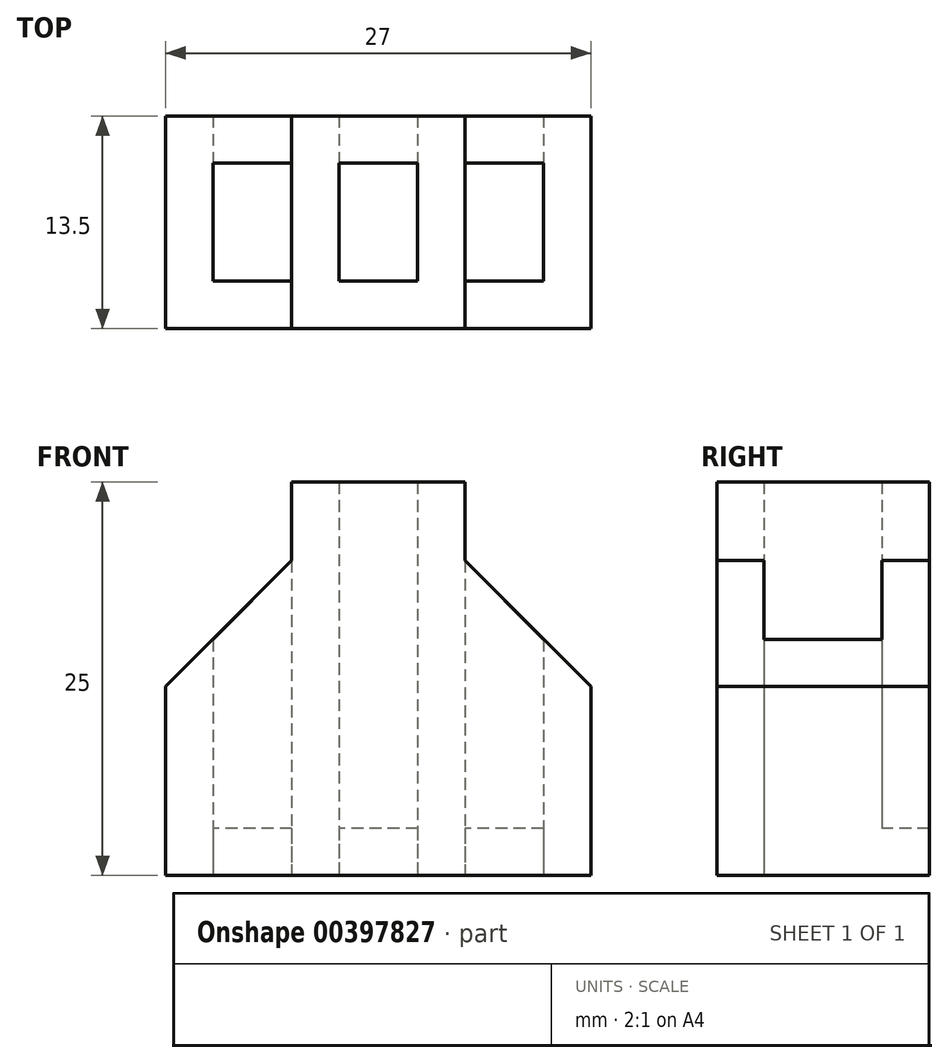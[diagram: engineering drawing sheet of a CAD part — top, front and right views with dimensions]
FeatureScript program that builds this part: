
annotation { "Feature Type Name" : "Feature", "Feature Type Description" : "" }
export const myFeature = defineFeature(function(context is Context, id is Id, definition is map)
    precondition{}
    {
        {
            var Q0;
            Q0=qCreatedBy(makeId("Top.planeOp"),FACE);
            var sketch = newSketch(context, id + "F0", { "sketchPlane" : qUnion([Q0])});
            skLineSegment(sketch, "E0.bottom", {"start": v(-2.5, -3.75) * mm, "end": v(2.5, -3.75) * mm});
            skLineSegment(sketch, "E0.top", {"start": v(-2.5, 3.75) * mm, "end": v(2.5, 3.75) * mm});
            skLineSegment(sketch, "E0.left", {"start": v(-2.5, -3.75) * mm, "end": v(-2.5, 3.75) * mm});
            skLineSegment(sketch, "E0.right", {"start": v(2.5, -3.75) * mm, "end": v(2.5, 3.75) * mm});
            skPoint(sketch, "E0.middle", {"position": v(0, 0) * mm});
            skLineSegment(sketch, "E1.0", {"start": v(-5.5, 6.75) * mm, "end": v(5.5, 6.75) * mm});
            skLineSegment(sketch, "E1.1", {"start": v(-5.5, -3.75) * mm, "end": v(-5.5, 3.75) * mm});
            skLineSegment(sketch, "E1.2", {"start": v(-5.5, -6.75) * mm, "end": v(5.5, -6.75) * mm});
            skLineSegment(sketch, "E1.3", {"start": v(5.5, -3.75) * mm, "end": v(5.5, 3.75) * mm});
            skLineSegment(sketch, "E2", {"start": v(-5.5, 3.75) * mm, "end": v(-10.5, 3.75) * mm});
            skLineSegment(sketch, "E3", {"start": v(-10.5, 3.75) * mm, "end": v(-10.5, -3.75) * mm});
            skLineSegment(sketch, "E4", {"start": v(-10.5, -3.75) * mm, "end": v(-5.5, -3.75) * mm});
            skLineSegment(sketch, "E5.0", {"start": v(-13.5, -6.75) * mm, "end": v(-5.5, -6.75) * mm});
            skLineSegment(sketch, "E5.1", {"start": v(-13.5, 6.75) * mm, "end": v(-13.5, -6.75) * mm});
            skLineSegment(sketch, "E5.2", {"start": v(-5.5, 6.75) * mm, "end": v(-13.5, 6.75) * mm});
            skLineSegment(sketch, "E6.MirrorCS", {"start": v(5.5, 3.75) * mm, "end": v(10.5, 3.75) * mm});
            skLineSegment(sketch, "E7.MirrorCS", {"start": v(10.5, -3.75) * mm, "end": v(5.5, -3.75) * mm});
            skLineSegment(sketch, "E8.MirrorCS", {"start": v(10.5, 3.75) * mm, "end": v(10.5, -3.75) * mm});
            skLineSegment(sketch, "E9.MirrorCS", {"start": v(13.5, -6.75) * mm, "end": v(5.5, -6.75) * mm});
            skLineSegment(sketch, "E10.MirrorCS", {"start": v(13.5, 6.75) * mm, "end": v(13.5, -6.75) * mm});
            skLineSegment(sketch, "E11.MirrorCS", {"start": v(5.5, 6.75) * mm, "end": v(13.5, 6.75) * mm});
            skLineSegment(sketch, "E12", {"start": v(5.5, 3.75) * mm, "end": v(5.5, 6.75) * mm});
            skLineSegment(sketch, "E13", {"start": v(5.5, -3.75) * mm, "end": v(5.5, -6.75) * mm});
            skLineSegment(sketch, "E14", {"start": v(-5.5, -3.75) * mm, "end": v(-5.5, -6.75) * mm});
            skLineSegment(sketch, "E15", {"start": v(-5.5, 3.75) * mm, "end": v(-5.5, 6.75) * mm});
            skSolve(sketch);
        }
        {
            var Q0;
            Q0=makeQuery(id+"F0.imprint","IMPRINT",FACE,{"disambiguationData":[TD([[makeQuery(id+"F0.imprint","IMPRINT",EDGE,{"derivedFrom":sQuery(id+"F0.wireOp",EDGE,"E0.bottom")}),-1.0]])]});
            extrude(context, id + "F1", {"entities" : qUnion([Q0]), "depth" : 25 * mm});
        }
        {
            var Q0;
            Q0=makeQuery(id+"F0.imprint","IMPRINT",FACE,{"disambiguationData":[TD([[makeQuery(id+"F0.imprint","IMPRINT",EDGE,{"derivedFrom":sQuery(id+"F0.wireOp",EDGE,"E2")}),-1.0]])]});
            var Q1;
            Q1=makeQuery(id+"F0.imprint","IMPRINT",FACE,{"disambiguationData":[TD([[makeQuery(id+"F0.imprint","IMPRINT",EDGE,{"derivedFrom":sQuery(id+"F0.wireOp",EDGE,"E6.MirrorCS")}),1.0]])]});
            extrude(context, id + "F2", {"entities" : qUnion([Q0, Q1]), "operationType" : NewBodyOperationType.ADD, "depth" : 20 * mm});
        }
        {
            var Q0;
            Q0=makeQuery(id+"F2.boolean.opBoolean","MERGE",FACE,{"derivedFrom":[makeQuery(id+"F1.opExtrude","SWEPT_FACE",FACE,{"disambiguationData":[OSD([sQuery(id+"F0.wireOp",EDGE,"E1.2")])]}),makeQuery(id+"F2.opExtrude","SWEPT_FACE",FACE,{"disambiguationData":[OSD([sQuery(id+"F0.wireOp",EDGE,"E5.0")])]}),makeQuery(id+"F2.opExtrude","SWEPT_FACE",FACE,{"disambiguationData":[OSD([sQuery(id+"F0.wireOp",EDGE,"E9.MirrorCS")])]})]});
            var sketch = newSketch(context, id + "F3", { "sketchPlane" : qUnion([Q0])});
            skLineSegment(sketch, "E16", {"start": v(-5.5, 20) * mm, "end": v(-13.5, 12) * mm});
            skLineSegment(sketch, "E17.MirrorCS", {"start": v(5.5, 20) * mm, "end": v(13.5, 12) * mm});
            skSolve(sketch);
        }
        {
            var Q0;
            {var subQ0=sQuery(id+"F3.wireOp",EDGE,"E16");Q0=makeQuery(id+"F3.imprint","IMPRINT",FACE,{"disambiguationData":[TD([[makeQuery(id+"F3.imprint","IMPRINT",EDGE,{"derivedFrom":subQ0}),-1.0]])]});}
            var Q1;
            {var subQ0=sQuery(id+"F3.wireOp",EDGE,"E17.MirrorCS");Q1=makeQuery(id+"F3.imprint","IMPRINT",FACE,{"disambiguationData":[TD([[makeQuery(id+"F3.imprint","IMPRINT",EDGE,{"derivedFrom":subQ0}),1.0]])]});}
            extrude(context, id + "F4", {"entities" : qUnion([Q0, Q1]), "operationType" : NewBodyOperationType.REMOVE, "oppositeDirection" : true, "depth" : 25 * mm});
        }
        {
            var Q0;
            Q0=qCreatedBy(makeId("Front.planeOp"),FACE);
            var sketch = newSketch(context, id + "F5", { "sketchPlane" : qUnion([Q0])});
            skLineSegment(sketch, "E18.bottom", {"start": v(-10.5, 0) * mm, "end": v(-5.5, 0) * mm});
            skLineSegment(sketch, "E18.top", {"start": v(-10.5, 3) * mm, "end": v(-5.5, 3) * mm});
            skLineSegment(sketch, "E18.left", {"start": v(-10.5, 0) * mm, "end": v(-10.5, 3) * mm});
            skLineSegment(sketch, "E18.right", {"start": v(-5.5, 0) * mm, "end": v(-5.5, 3) * mm});
            skLineSegment(sketch, "E19.bottom", {"start": v(-2.5, 0) * mm, "end": v(2.5, 0) * mm});
            skLineSegment(sketch, "E19.top", {"start": v(-2.5, 3) * mm, "end": v(2.5, 3) * mm});
            skLineSegment(sketch, "E19.left", {"start": v(-2.5, 0) * mm, "end": v(-2.5, 3) * mm});
            skLineSegment(sketch, "E19.right", {"start": v(2.5, 0) * mm, "end": v(2.5, 3) * mm});
            skLineSegment(sketch, "E20.bottom", {"start": v(5.5, 0) * mm, "end": v(10.5, 0) * mm});
            skLineSegment(sketch, "E20.top", {"start": v(5.5, 3) * mm, "end": v(10.5, 3) * mm});
            skLineSegment(sketch, "E20.left", {"start": v(5.5, 0) * mm, "end": v(5.5, 3) * mm});
            skLineSegment(sketch, "E20.right", {"start": v(10.5, 0) * mm, "end": v(10.5, 3) * mm});
            skSolve(sketch);
        }
        {
            var Q0;
            Q0=qSketchRegion(id+"F5",true);
            extrude(context, id + "F6", {"entities" : qUnion([Q0]), "operationType" : NewBodyOperationType.REMOVE, "oppositeDirection" : true, "depth" : 25 * mm});
        }
    });
